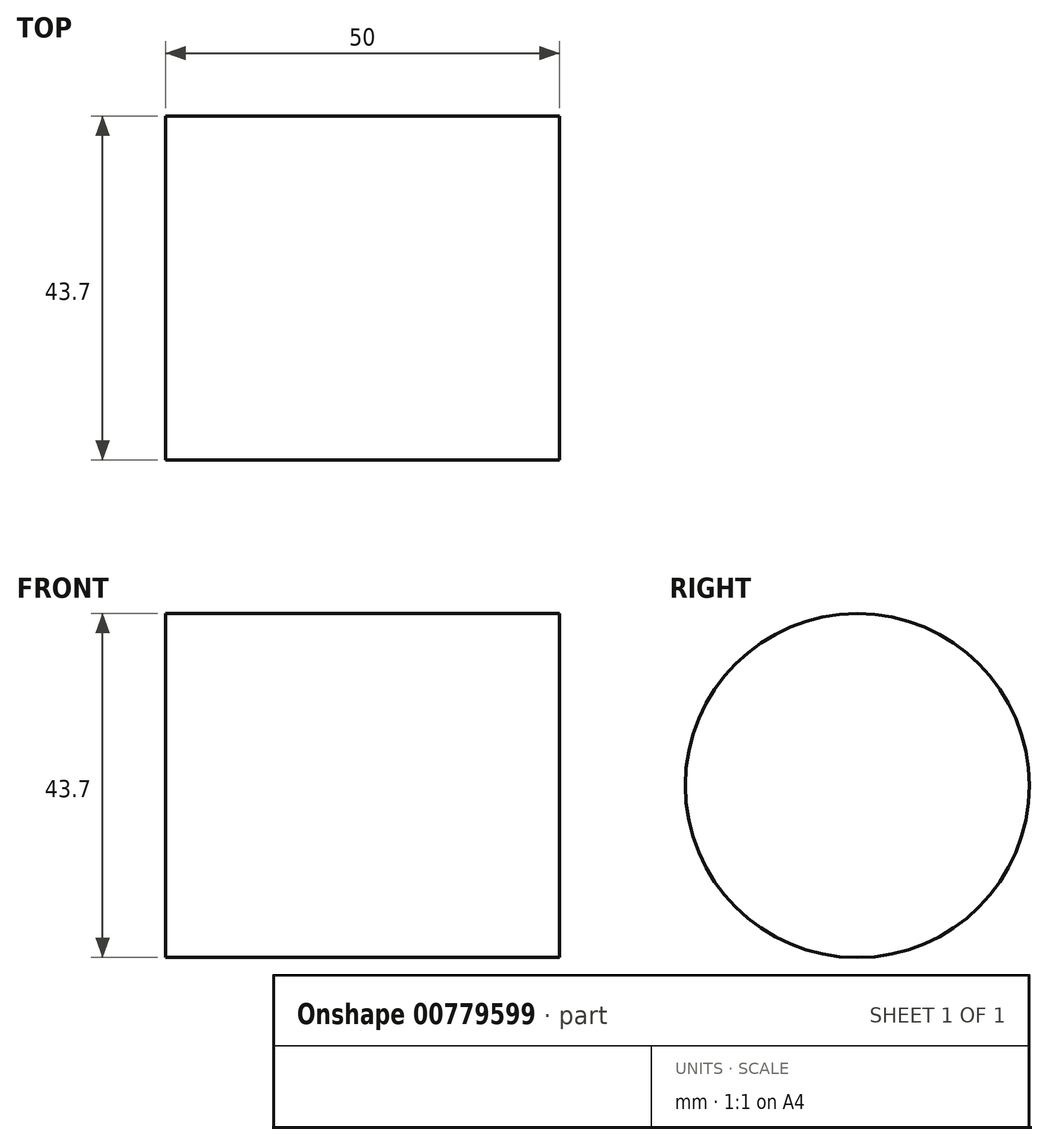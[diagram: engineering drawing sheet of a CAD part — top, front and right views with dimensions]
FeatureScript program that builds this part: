
annotation { "Feature Type Name" : "Feature", "Feature Type Description" : "" }
export const myFeature = defineFeature(function(context is Context, id is Id, definition is map)
    precondition{}
    {
        {
            var Q0;
            Q0=qCreatedBy(makeId("Right.planeOp"),FACE);
            var sketch = newSketch(context, id + "F0", { "sketchPlane" : qUnion([Q0])});
            skCircle(sketch, "E0", {"center": v(0, 0) * mm, "radius": 21.85 * mm});
            skSolve(sketch);
        }
        {
            var Q0;
            Q0 = qSketchRegion(id + "F0", true);
            extrude(context, id + "F1", {"entities" : qUnion([Q0]), "depth" : 50 * mm, "offsetDistance" : 25 * mm});
        }
    });
